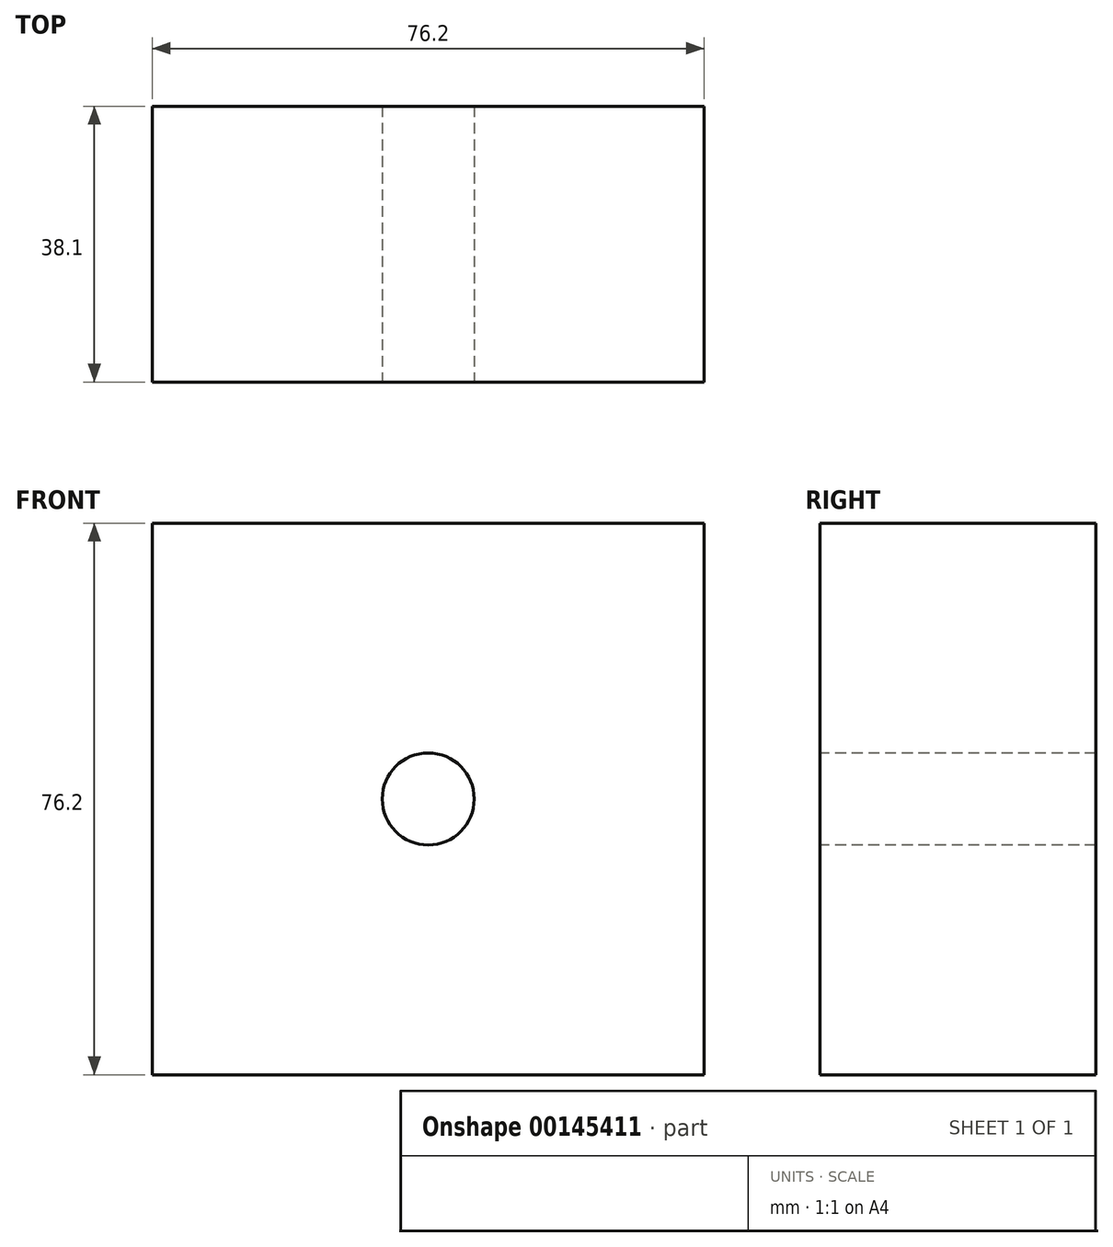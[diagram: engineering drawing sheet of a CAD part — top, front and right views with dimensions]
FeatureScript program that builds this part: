
annotation { "Feature Type Name" : "Feature", "Feature Type Description" : "" }
export const myFeature = defineFeature(function(context is Context, id is Id, definition is map)
    precondition{}
    {
        {
            var Q0;
            Q0=qCreatedBy(makeId("Front.planeOp"),FACE);
            var sketch = newSketch(context, id + "F0", { "sketchPlane" : qUnion([Q0])});
            skLineSegment(sketch, "E0.bottom", {"start": v(-38.1, 38.1) * mm, "end": v(38.1, 38.1) * mm});
            skLineSegment(sketch, "E0.top", {"start": v(-38.1, -38.1) * mm, "end": v(38.1, -38.1) * mm});
            skLineSegment(sketch, "E0.left", {"start": v(-38.1, 38.1) * mm, "end": v(-38.1, -38.1) * mm});
            skLineSegment(sketch, "E0.right", {"start": v(38.1, 38.1) * mm, "end": v(38.1, -38.1) * mm});
            skPoint(sketch, "E0.middle", {"position": v(0, 0) * mm});
            skSolve(sketch);
        }
        {
            var Q0;
            Q0 = qSketchRegion(id + "F0", true);
            extrude(context, id + "F1", {"entities" : qUnion([Q0]), "endBound" : BoundingType.SYMMETRIC, "depth" : 38.1 * mm});
        }
        {
            var Q0;
            Q0=qCreatedBy(makeId("Front.planeOp"),FACE);
            cPlane(context, id + "F2", {"entities" : qUnion([Q0]), "cplaneType" : CPlaneType.OFFSET, "offset" : 25.4 * mm, "width" : 152.4 * mm, "height" : 152.4 * mm});
        }
        {
            var Q0;
            Q0=qCreatedBy(id+"F2.planeOp",FACE);
            var sketch = newSketch(context, id + "F3", { "sketchPlane" : qUnion([Q0])});
            skPoint(sketch, "E1", {"position": v(0, 0) * mm});
            skSolve(sketch);
        }
        {
            var Q0;
            Q0=sQuery(id+"F3.wireOp",VERTEX,"E1");
            var Q1;
            Q1=makeQuery(id+"F1.opExtrude","SWEPT_BODY",BODY,{"disambiguationData":[OSD([sQuery(id+"F0.wireOp",EDGE,"E0.bottom"),sQuery(id+"F0.wireOp",EDGE,"E0.top"),sQuery(id+"F0.wireOp",EDGE,"E0.left"),sQuery(id+"F0.wireOp",EDGE,"E0.right")])]});
            hole(context, id + "F4", {"style" : HoleStyle.SIMPLE, "endStyle" : HoleEndStyle.BLIND, "holeDiameter" : 12.7 * mm, "holeDepth" : 609.6 * mm, "startFromSketch" : true, "locations" : qUnion([Q0]), "scope" : qUnion([Q1])});
        }
    });
